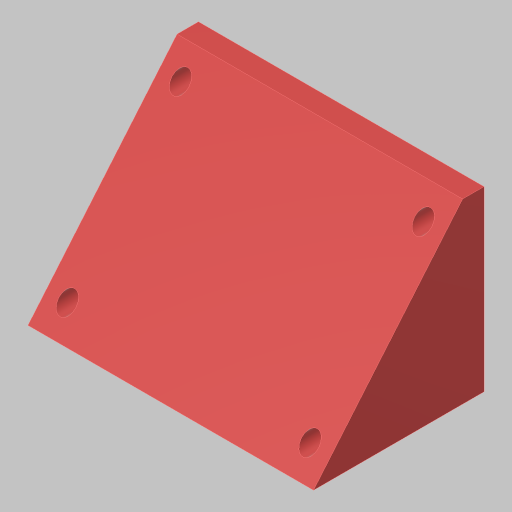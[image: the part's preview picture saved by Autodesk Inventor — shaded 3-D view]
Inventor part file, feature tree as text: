
AUTODESK INVENTOR PART (.ipt)
format: ipt  version: 2023.5 (Build 275446000, 446)  size: 109,568 bytes
history: native  units: in
note: dims shown in document units (in); Inventor stores cm internally (conversion verified against a paired STEP export)
features: sketch x2, extrude x2, hole x1
ambient origin geometry x8: Origin, YZ Plane, XZ Plane, XY Plane, X Axis, Y Axis, Z Axis, Center Point
bodies: Solid1 (feature_tree)
feature tree (5):
  sketch  "Sketch1"  dims[d0=2.8346in d1=1.5748in]
  extrude  "Extrusion1"  Depth=1.5748in
  extrude  "Extrusion2"  Depth=0.25in
  hole  "Hole2"  [1 undecoded]
  sketch  "Sketch2"  dims[d2=0.25in d3=0.25in d4=0.25in d5=0.0in d13=0.2749in d15=0.25in d16=0.0in d17=0.201in d18=0.75in d19=0.375in d20=0.25in d21=0.5635in d22=1.0in d23=0.8108in]
note: 1 required parameter value undecoded (feature->parameter linkage not recoverable at this tier; creation-order binding heuristic only, values carry confidence <= 0.55)
